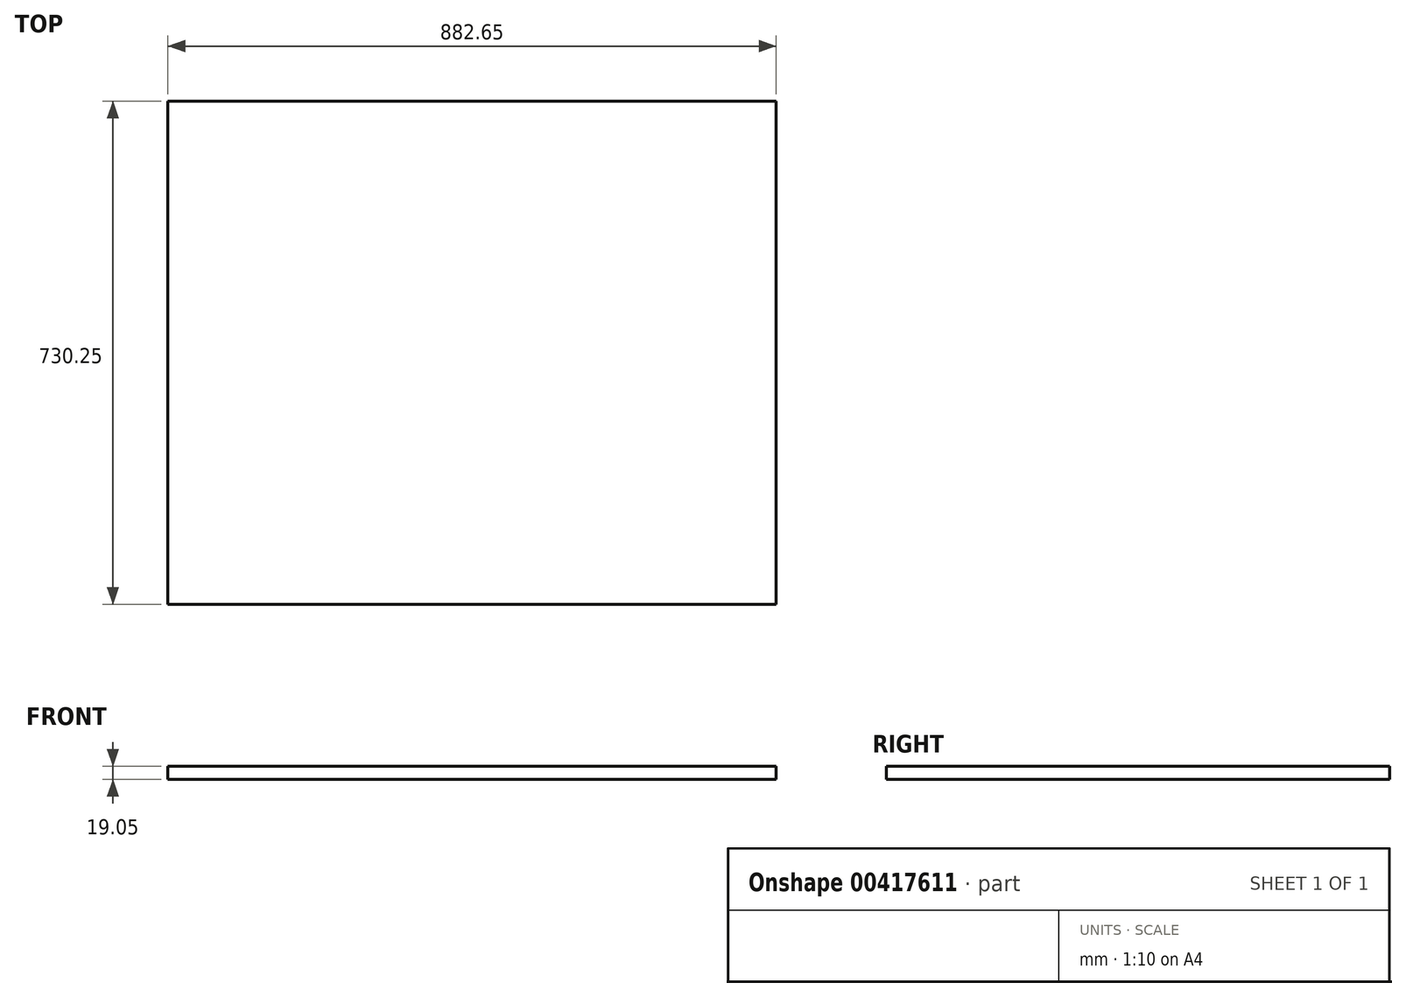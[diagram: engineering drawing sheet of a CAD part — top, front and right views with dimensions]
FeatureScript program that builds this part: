
annotation { "Feature Type Name" : "Feature", "Feature Type Description" : "" }
export const myFeature = defineFeature(function(context is Context, id is Id, definition is map)
    precondition{}
    {
        {
            var Q0;
            Q0=qCreatedBy(makeId("Top.planeOp"),FACE);
            var sketch = newSketch(context, id + "F0", { "sketchPlane" : qUnion([Q0])});
            skLineSegment(sketch, "E0.bottom", {"start": v(-438.55, 499.47) * mm, "end": v(444.1, 499.47) * mm});
            skLineSegment(sketch, "E0.top", {"start": v(-438.55, -230.78) * mm, "end": v(444.1, -230.78) * mm});
            skLineSegment(sketch, "E0.left", {"start": v(-438.55, 499.47) * mm, "end": v(-438.55, -230.78) * mm});
            skLineSegment(sketch, "E0.right", {"start": v(444.1, 499.47) * mm, "end": v(444.1, -230.78) * mm});
            skSolve(sketch);
        }
        {
            var Q0;
            Q0=makeQuery(id+"F0.imprint","IMPRINT",FACE,{"disambiguationData":[TD([[makeQuery(id+"F0.imprint","IMPRINT",EDGE,{"derivedFrom":sQuery(id+"F0.wireOp",EDGE,"E0.bottom")}),-1.0]])]});
            extrude(context, id + "F1", {"entities" : qUnion([Q0]), "depth" : 19.05 * mm});
        }
    });
